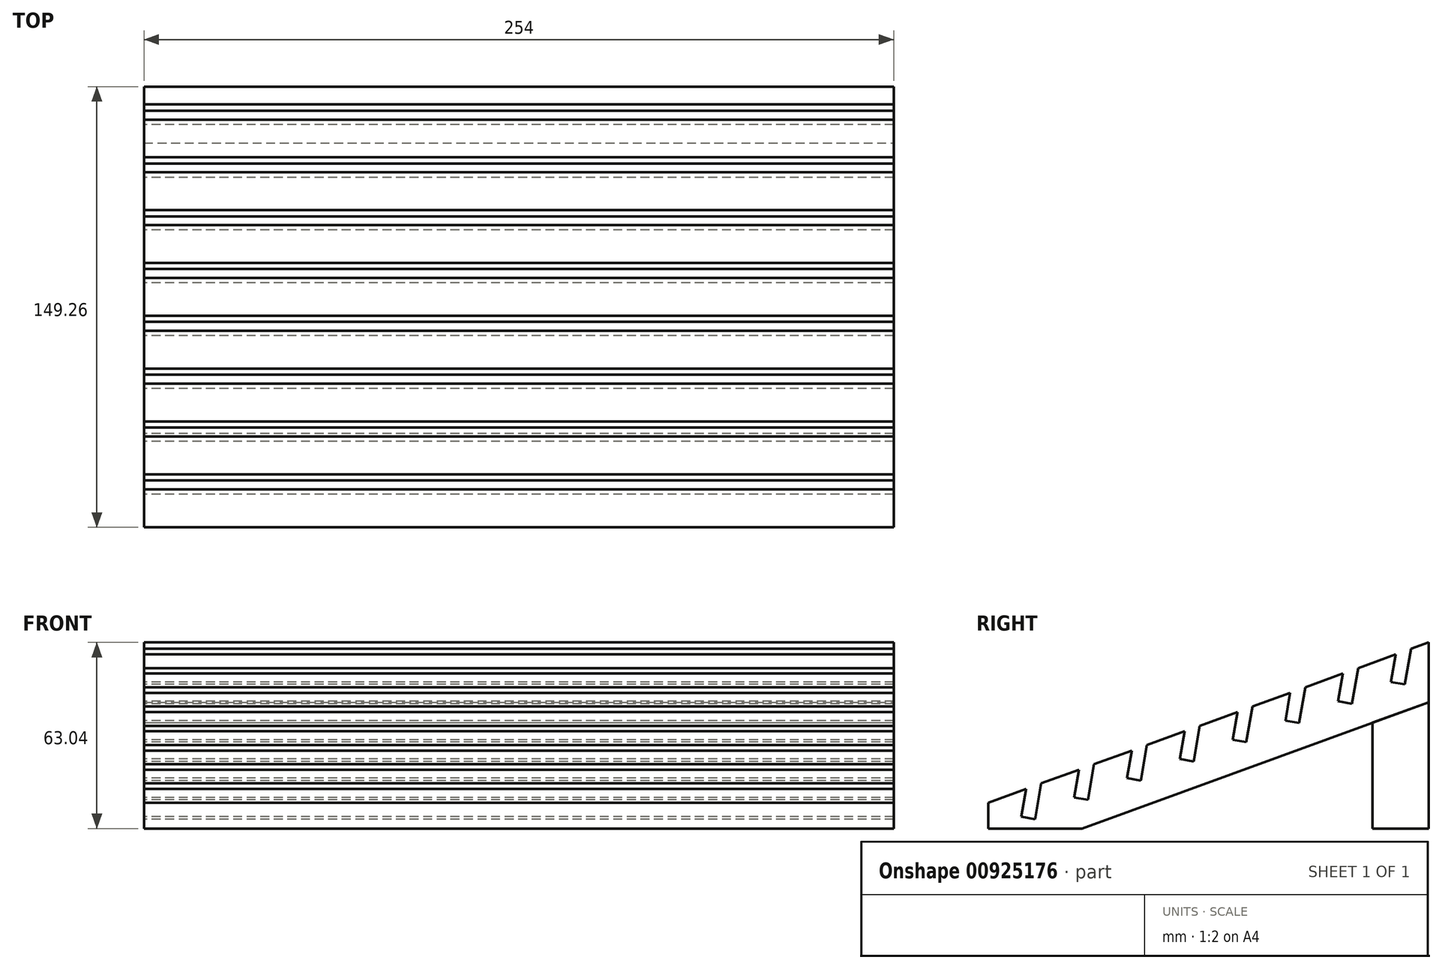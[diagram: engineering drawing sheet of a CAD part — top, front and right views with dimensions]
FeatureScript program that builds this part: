
annotation { "Feature Type Name" : "Feature", "Feature Type Description" : "" }
export const myFeature = defineFeature(function(context is Context, id is Id, definition is map)
    precondition{}
    {
        {
            var Q0;
            Q0=qCreatedBy(makeId("Right.planeOp"),FACE);
            var sketch = newSketch(context, id + "F0", { "sketchPlane" : qUnion([Q0])});
            skLineSegment(sketch, "E0", {"start": v(0, 0) * mm, "end": v(-31.75, 0) * mm});
            skLineSegment(sketch, "E1", {"start": v(-31.75, 8.72) * mm, "end": v(-18.93, 13.38) * mm});
            skLineSegment(sketch, "E2", {"start": v(117.51, 63.04) * mm, "end": v(117.51, 42.77) * mm});
            skLineSegment(sketch, "E3", {"start": v(117.51, 42.77) * mm, "end": v(0, 0) * mm});
            skLineSegment(sketch, "E4", {"start": v(-18.93, 13.38) * mm, "end": v(-20.58, 4) * mm});
            skLineSegment(sketch, "E5", {"start": v(-20.58, 4) * mm, "end": v(-15.9, 3.17) * mm});
            skLineSegment(sketch, "E6", {"start": v(-15.9, 3.17) * mm, "end": v(-13.76, 15.26) * mm});
            skLineSegment(sketch, "E7.trimOffspring", {"start": v(-13.76, 15.26) * mm, "end": v(-1.03, 19.9) * mm});
            skLineSegment(sketch, "E8.1.0.0", {"start": v(-1.03, 19.9) * mm, "end": v(-2.68, 10.52) * mm});
            skLineSegment(sketch, "E8.1.0.1", {"start": v(2, 9.7) * mm, "end": v(4.14, 21.78) * mm});
            skLineSegment(sketch, "E8.1.0.2", {"start": v(-2.68, 10.52) * mm, "end": v(2, 9.7) * mm});
            skLineSegment(sketch, "E8.2.0.0", {"start": v(16.87, 26.41) * mm, "end": v(15.22, 17.03) * mm});
            skLineSegment(sketch, "E8.2.0.1", {"start": v(19.9, 16.2) * mm, "end": v(22.04, 28.3) * mm});
            skLineSegment(sketch, "E8.2.0.2", {"start": v(15.22, 17.03) * mm, "end": v(19.9, 16.2) * mm});
            skLineSegment(sketch, "E8.direction1", {"start": v(-20.58, 4) * mm, "end": v(-2.68, 10.52) * mm, "construction": true});
            skLineSegment(sketch, "E9.0.3.0", {"start": v(34.77, 32.93) * mm, "end": v(33.12, 23.55) * mm});
            skLineSegment(sketch, "E9.3.3.0", {"start": v(37.8, 22.72) * mm, "end": v(39.94, 34.8) * mm});
            skLineSegment(sketch, "E9.6.3.0", {"start": v(33.12, 23.55) * mm, "end": v(37.8, 22.72) * mm});
            skLineSegment(sketch, "E9.0.4.0", {"start": v(52.67, 39.44) * mm, "end": v(51.02, 30.06) * mm});
            skLineSegment(sketch, "E9.3.4.0", {"start": v(55.7, 29.24) * mm, "end": v(57.84, 41.33) * mm});
            skLineSegment(sketch, "E9.6.4.0", {"start": v(51.02, 30.06) * mm, "end": v(55.7, 29.24) * mm});
            skLineSegment(sketch, "E9.0.5.0", {"start": v(70.57, 45.96) * mm, "end": v(68.92, 36.58) * mm});
            skLineSegment(sketch, "E9.3.5.0", {"start": v(73.61, 35.75) * mm, "end": v(75.74, 47.84) * mm});
            skLineSegment(sketch, "E9.6.5.0", {"start": v(68.92, 36.58) * mm, "end": v(73.61, 35.75) * mm});
            skLineSegment(sketch, "E9.0.6.0", {"start": v(88.48, 52.48) * mm, "end": v(86.82, 43.1) * mm});
            skLineSegment(sketch, "E9.3.6.0", {"start": v(91.51, 42.27) * mm, "end": v(93.64, 54.36) * mm});
            skLineSegment(sketch, "E9.6.6.0", {"start": v(86.82, 43.1) * mm, "end": v(91.51, 42.27) * mm});
            skLineSegment(sketch, "E9.0.7.0", {"start": v(106.38, 59) * mm, "end": v(104.72, 49.61) * mm});
            skLineSegment(sketch, "E9.3.7.0", {"start": v(109.41, 48.78) * mm, "end": v(111.54, 60.87) * mm});
            skLineSegment(sketch, "E9.6.7.0", {"start": v(104.72, 49.61) * mm, "end": v(109.41, 48.78) * mm});
            skLineSegment(sketch, "E10", {"start": v(117.51, 42.77) * mm, "end": v(124.03, 45.14) * mm, "construction": true});
            skLineSegment(sketch, "E11", {"start": v(117.51, 63.04) * mm, "end": v(124.03, 45.14) * mm, "construction": true});
            skLineSegment(sketch, "E12.trimOffspring", {"start": v(111.54, 60.87) * mm, "end": v(117.51, 63.04) * mm});
            skLineSegment(sketch, "E13.trimOffspring", {"start": v(93.64, 54.36) * mm, "end": v(106.38, 59) * mm});
            skLineSegment(sketch, "E14.trimOffspring", {"start": v(75.74, 47.84) * mm, "end": v(88.48, 52.48) * mm});
            skLineSegment(sketch, "E15.trimOffspring", {"start": v(57.84, 41.33) * mm, "end": v(70.57, 45.96) * mm});
            skLineSegment(sketch, "E16.trimOffspring", {"start": v(39.94, 34.8) * mm, "end": v(52.67, 39.44) * mm});
            skLineSegment(sketch, "E17.trimOffspring", {"start": v(22.04, 28.3) * mm, "end": v(34.77, 32.93) * mm});
            skLineSegment(sketch, "E18.trimOffspring", {"start": v(4.14, 21.78) * mm, "end": v(16.87, 26.41) * mm});
            skLineSegment(sketch, "E19", {"start": v(0, 0) * mm, "end": v(-49.18, -17.9) * mm, "construction": true});
            skLineSegment(sketch, "E20", {"start": v(-55.7, 0) * mm, "end": v(-49.18, -17.9) * mm, "construction": true});
            skLineSegment(sketch, "E21", {"start": v(-31.75, 8.72) * mm, "end": v(-31.75, 0) * mm});
            skSolve(sketch);
        }
        {
            var Q0;
            Q0 = qSketchRegion(id + "F0", true);
            extrude(context, id + "F1", {"entities" : qUnion([Q0]), "endBound" : BoundingType.SYMMETRIC, "depth" : 254 * mm, "offsetDistance" : 25.4 * mm});
        }
        {
            var Q0;
            Q0=makeQuery(id+"F1.opExtrude","CAP_FACE",FACE,{"disambiguationData":[OSD([sQuery(id+"F0.wireOp",EDGE,"E0"),sQuery(id+"F0.wireOp",EDGE,"E1"),sQuery(id+"F0.wireOp",EDGE,"E2"),sQuery(id+"F0.wireOp",EDGE,"E3"),sQuery(id+"F0.wireOp",EDGE,"E4"),sQuery(id+"F0.wireOp",EDGE,"E5"),sQuery(id+"F0.wireOp",EDGE,"E6"),sQuery(id+"F0.wireOp",EDGE,"E7.trimOffspring"),sQuery(id+"F0.wireOp",EDGE,"E8.1.0.0"),sQuery(id+"F0.wireOp",EDGE,"E8.1.0.1"),sQuery(id+"F0.wireOp",EDGE,"E8.1.0.2"),sQuery(id+"F0.wireOp",EDGE,"E8.2.0.0"),sQuery(id+"F0.wireOp",EDGE,"E8.2.0.1"),sQuery(id+"F0.wireOp",EDGE,"E8.2.0.2"),sQuery(id+"F0.wireOp",EDGE,"E9.0.3.0"),sQuery(id+"F0.wireOp",EDGE,"E9.3.3.0"),sQuery(id+"F0.wireOp",EDGE,"E9.6.3.0"),sQuery(id+"F0.wireOp",EDGE,"E9.0.4.0"),sQuery(id+"F0.wireOp",EDGE,"E9.3.4.0"),sQuery(id+"F0.wireOp",EDGE,"E9.6.4.0"),sQuery(id+"F0.wireOp",EDGE,"E9.0.5.0"),sQuery(id+"F0.wireOp",EDGE,"E9.3.5.0"),sQuery(id+"F0.wireOp",EDGE,"E9.6.5.0"),sQuery(id+"F0.wireOp",EDGE,"E9.0.6.0"),sQuery(id+"F0.wireOp",EDGE,"E9.3.6.0"),sQuery(id+"F0.wireOp",EDGE,"E9.6.6.0"),sQuery(id+"F0.wireOp",EDGE,"E9.0.7.0"),sQuery(id+"F0.wireOp",EDGE,"E9.3.7.0"),sQuery(id+"F0.wireOp",EDGE,"E9.6.7.0"),sQuery(id+"F0.wireOp",EDGE,"E12.trimOffspring"),sQuery(id+"F0.wireOp",EDGE,"E13.trimOffspring"),sQuery(id+"F0.wireOp",EDGE,"E14.trimOffspring"),sQuery(id+"F0.wireOp",EDGE,"E15.trimOffspring"),sQuery(id+"F0.wireOp",EDGE,"E16.trimOffspring"),sQuery(id+"F0.wireOp",EDGE,"E17.trimOffspring"),sQuery(id+"F0.wireOp",EDGE,"E18.trimOffspring")])],"isStart":false});
            var sketch = newSketch(context, id + "F2", { "sketchPlane" : qUnion([Q0])});
            skLineSegment(sketch, "E22", {"start": v(117.51, 42.77) * mm, "end": v(117.51, 0) * mm});
            skLineSegment(sketch, "E23", {"start": v(117.51, 0) * mm, "end": v(98.46, 0) * mm});
            skLineSegment(sketch, "E24", {"start": v(98.46, 0) * mm, "end": v(98.46, 35.84) * mm});
            skLineSegment(sketch, "E25", {"start": v(98.46, 35.84) * mm, "end": v(117.51, 42.77) * mm});
            skSolve(sketch);
        }
        {
            var Q0;
            Q0 = qSketchRegion(id + "F2", true);
            var Q1;
            Q1=makeQuery(id+"F1.opExtrude","CAP_FACE",FACE,{"disambiguationData":[OSD([sQuery(id+"F0.wireOp",EDGE,"E0"),sQuery(id+"F0.wireOp",EDGE,"E1"),sQuery(id+"F0.wireOp",EDGE,"E2"),sQuery(id+"F0.wireOp",EDGE,"E3"),sQuery(id+"F0.wireOp",EDGE,"E4"),sQuery(id+"F0.wireOp",EDGE,"E5"),sQuery(id+"F0.wireOp",EDGE,"E6"),sQuery(id+"F0.wireOp",EDGE,"E7.trimOffspring"),sQuery(id+"F0.wireOp",EDGE,"E8.1.0.0"),sQuery(id+"F0.wireOp",EDGE,"E8.1.0.1"),sQuery(id+"F0.wireOp",EDGE,"E8.1.0.2"),sQuery(id+"F0.wireOp",EDGE,"E8.2.0.0"),sQuery(id+"F0.wireOp",EDGE,"E8.2.0.1"),sQuery(id+"F0.wireOp",EDGE,"E8.2.0.2"),sQuery(id+"F0.wireOp",EDGE,"E9.0.3.0"),sQuery(id+"F0.wireOp",EDGE,"E9.3.3.0"),sQuery(id+"F0.wireOp",EDGE,"E9.6.3.0"),sQuery(id+"F0.wireOp",EDGE,"E9.0.4.0"),sQuery(id+"F0.wireOp",EDGE,"E9.3.4.0"),sQuery(id+"F0.wireOp",EDGE,"E9.6.4.0"),sQuery(id+"F0.wireOp",EDGE,"E9.0.5.0"),sQuery(id+"F0.wireOp",EDGE,"E9.3.5.0"),sQuery(id+"F0.wireOp",EDGE,"E9.6.5.0"),sQuery(id+"F0.wireOp",EDGE,"E9.0.6.0"),sQuery(id+"F0.wireOp",EDGE,"E9.3.6.0"),sQuery(id+"F0.wireOp",EDGE,"E9.6.6.0"),sQuery(id+"F0.wireOp",EDGE,"E9.0.7.0"),sQuery(id+"F0.wireOp",EDGE,"E9.3.7.0"),sQuery(id+"F0.wireOp",EDGE,"E9.6.7.0"),sQuery(id+"F0.wireOp",EDGE,"E12.trimOffspring"),sQuery(id+"F0.wireOp",EDGE,"E13.trimOffspring"),sQuery(id+"F0.wireOp",EDGE,"E14.trimOffspring"),sQuery(id+"F0.wireOp",EDGE,"E15.trimOffspring"),sQuery(id+"F0.wireOp",EDGE,"E16.trimOffspring"),sQuery(id+"F0.wireOp",EDGE,"E17.trimOffspring"),sQuery(id+"F0.wireOp",EDGE,"E18.trimOffspring")])],"isStart":true});
            extrude(context, id + "F3", {"entities" : qUnion([Q0]), "endBound" : BoundingType.UP_TO_SURFACE, "oppositeDirection" : true, "depth" : 25.4 * mm, "endBoundEntityFace" : qUnion([Q1]), "offsetDistance" : 25.4 * mm});
        }
    });
